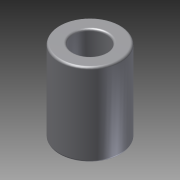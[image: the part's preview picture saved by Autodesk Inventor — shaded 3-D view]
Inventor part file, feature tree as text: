
AUTODESK INVENTOR PART (.ipt)
format: ipt  version: 2012 (Build 160160000, 160)  size: 111,616 bytes
history: native  units: mm
features: extrude x2, sketch x2, fillet x1
ambient origin geometry x8: Origin, YZ Plane, XZ Plane, XY Plane, X Axis, Y Axis, Z Axis, Center Point
feature tree (5):
  extrude  "Extrusion2"  Depth=8.0mm
  fillet  "Fillet1"  Radius=20.0mm
  extrude  "Extrusion3"  Depth=4.5mm TaperAngle=0.0deg
  sketch  "Sketch1"  dims[d0=14.9mm d3=8.0mm d4=20.0mm d5=0.0mm]
  sketch  "Sketch2"  dims[d6=0.5mm d7=4.5mm d8=0.0mm]
